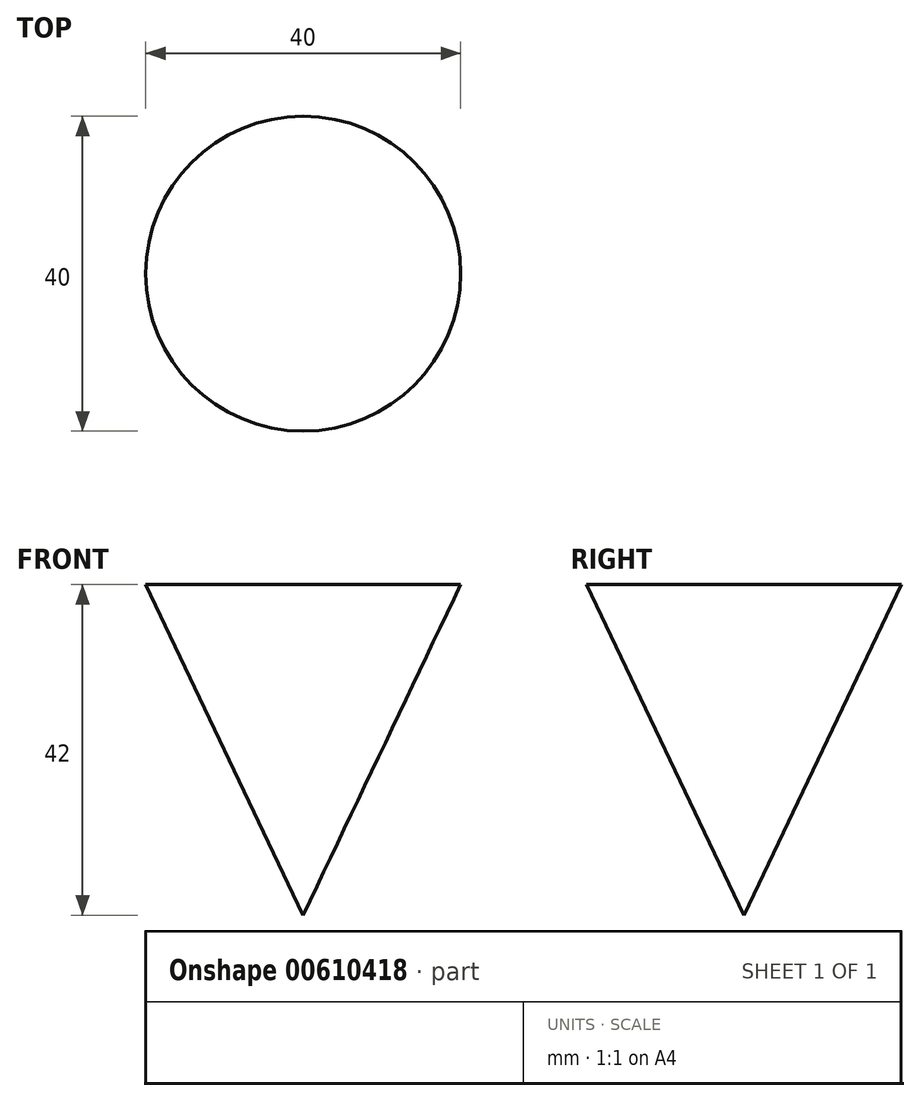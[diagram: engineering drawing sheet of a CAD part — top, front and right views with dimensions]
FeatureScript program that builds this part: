
annotation { "Feature Type Name" : "Feature", "Feature Type Description" : "" }
export const myFeature = defineFeature(function(context is Context, id is Id, definition is map)
    precondition{}
    {
        {
            var Q0;
            Q0=qCreatedBy(makeId("Front.planeOp"),FACE);
            var sketch = newSketch(context, id + "F0", { "sketchPlane" : qUnion([Q0])});
            skLineSegment(sketch, "E0", {"start": v(0, 0) * mm, "end": v(0, 42) * mm});
            skLineSegment(sketch, "E1", {"start": v(0, 42) * mm, "end": v(20, 42) * mm});
            skLineSegment(sketch, "E2", {"start": v(20, 42) * mm, "end": v(0, 0) * mm});
            skSolve(sketch);
        }
        {
            var Q0;
            Q0 = qSketchRegion(id + "F0", true);
            var Q1;
            Q1=sQuery(id+"F0.wireOp",EDGE,"E0");
            revolve(context, id + "F1", {"entities" : qUnion([Q0]), "axis" : qUnion([Q1]), "revolveType" : RevolveType.FULL});
        }
    });
